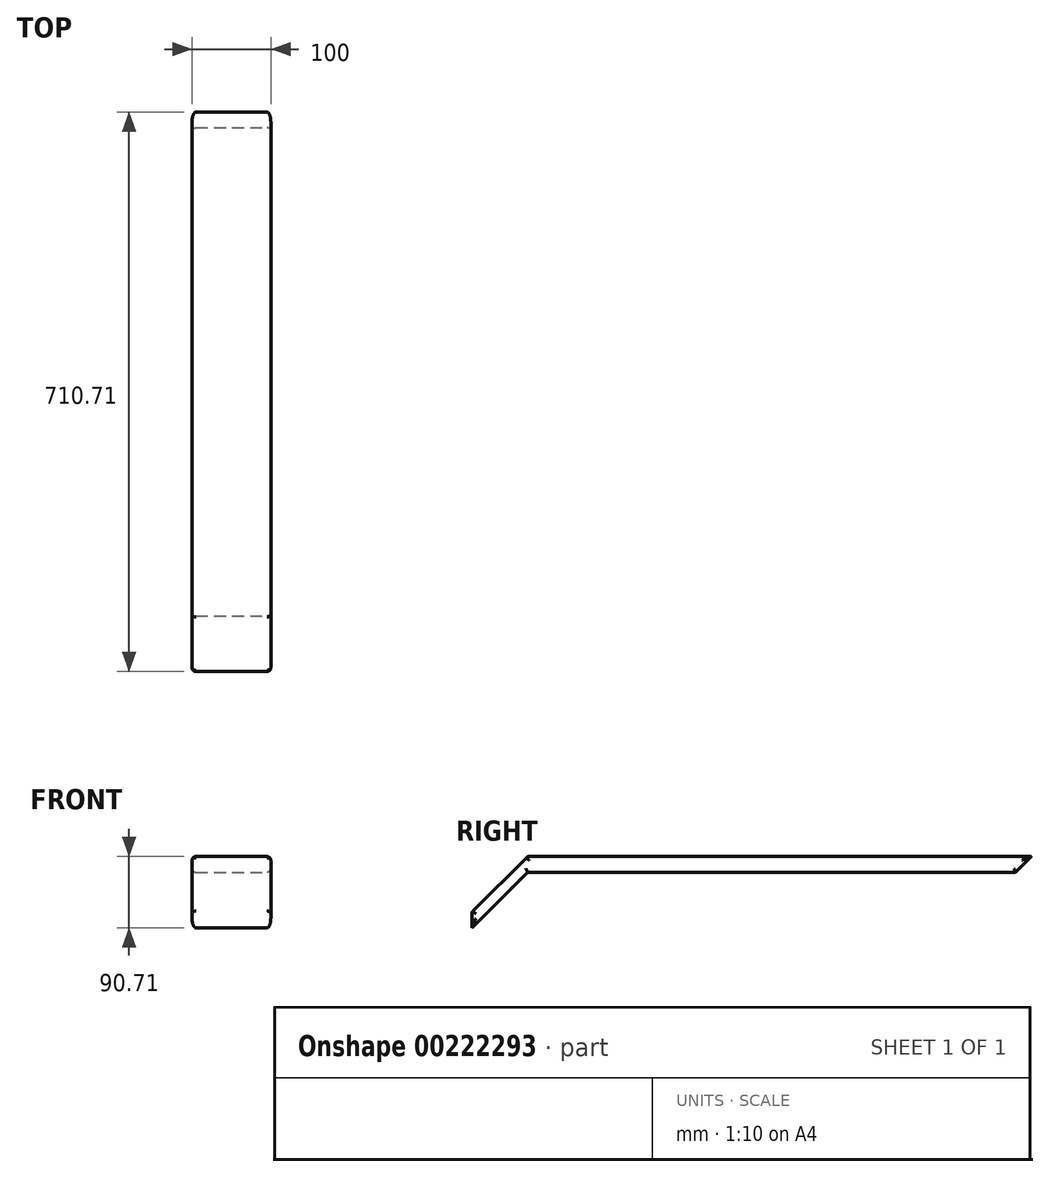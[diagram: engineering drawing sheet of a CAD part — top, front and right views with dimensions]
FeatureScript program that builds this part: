
annotation { "Feature Type Name" : "Feature", "Feature Type Description" : "" }
export const myFeature = defineFeature(function(context is Context, id is Id, definition is map)
    precondition{}
    {
        {
            var Q0;
            Q0=qCreatedBy(makeId("Right.planeOp"),FACE);
            var sketch = newSketch(context, id + "F0", { "sketchPlane" : qUnion([Q0])});
            skLineSegment(sketch, "E0.bottom", {"start": v(320, 10) * mm, "end": v(-320, 10) * mm});
            skLineSegment(sketch, "E0.top", {"start": v(300, -10) * mm, "end": v(-320, -10) * mm});
            skLineSegment(sketch, "E0.right", {"start": v(-320, 10) * mm, "end": v(-320, -10) * mm});
            skPoint(sketch, "E0.middle", {"position": v(0, 0) * mm});
            skLineSegment(sketch, "E1", {"start": v(-320, 10) * mm, "end": v(-390.71, -60.71) * mm});
            skLineSegment(sketch, "E2", {"start": v(-320, -10) * mm, "end": v(-390.71, -80.71) * mm});
            skLineSegment(sketch, "E3", {"start": v(-390.71, -60.71) * mm, "end": v(-390.71, -80.71) * mm});
            skLineSegment(sketch, "E4", {"start": v(320, 10) * mm, "end": v(300, -10) * mm});
            skSolve(sketch);
        }
        {
            var Q0;
            Q0 = qSketchRegion(id + "F0", true);
            extrude(context, id + "F1", {"entities" : qUnion([Q0]), "oppositeDirection" : true, "depth" : 100 * mm, "offsetDistance" : 25 * mm, "symmetric" : true});
        }
        {
            var Q0;
            Q0=makeQuery(id+"F1.opExtrude","CAP_FACE",FACE,{"disambiguationData":[OSD([sQuery(id+"F0.wireOp",EDGE,"E0.bottom"),sQuery(id+"F0.wireOp",EDGE,"E0.top"),sQuery(id+"F0.wireOp",EDGE,"E1"),sQuery(id+"F0.wireOp",EDGE,"E2"),sQuery(id+"F0.wireOp",EDGE,"E3"),sQuery(id+"F0.wireOp",EDGE,"E4")])],"isStart":true});
            var Q1;
            Q1=makeQuery(id+"F1.opExtrude","CAP_FACE",FACE,{"disambiguationData":[OSD([sQuery(id+"F0.wireOp",EDGE,"E0.bottom"),sQuery(id+"F0.wireOp",EDGE,"E0.top"),sQuery(id+"F0.wireOp",EDGE,"E1"),sQuery(id+"F0.wireOp",EDGE,"E2"),sQuery(id+"F0.wireOp",EDGE,"E3"),sQuery(id+"F0.wireOp",EDGE,"E4")])],"isStart":false});
            fillet(context, id + "F2", {"entities" : qUnion([Q0, Q1]), "radius" : 5 * mm, "tangentPropagation" : true, "allowEdgeOverflow" : false});
        }
        {
            var Q0;
            Q0=makeQuery(id+"F1.opExtrude","SWEPT_EDGE",EDGE,{"disambiguationData":[OSD([sQuery(id+"F0.wireOp",EDGE,"E0.bottom"),sQuery(id+"F0.wireOp",EDGE,"E0.right"),sQuery(id+"F0.wireOp",EDGE,"E1")])]});
            var Q1;
            Q1=makeQuery(id+"F1.opExtrude","SWEPT_EDGE",EDGE,{"disambiguationData":[OSD([sQuery(id+"F0.wireOp",EDGE,"E1"),sQuery(id+"F0.wireOp",EDGE,"E3")])]});
            fillet(context, id + "F3", {"entities" : qUnion([Q0, Q1]), "radius" : 5 * mm, "tangentPropagation" : true, "allowEdgeOverflow" : false});
        }
    });
